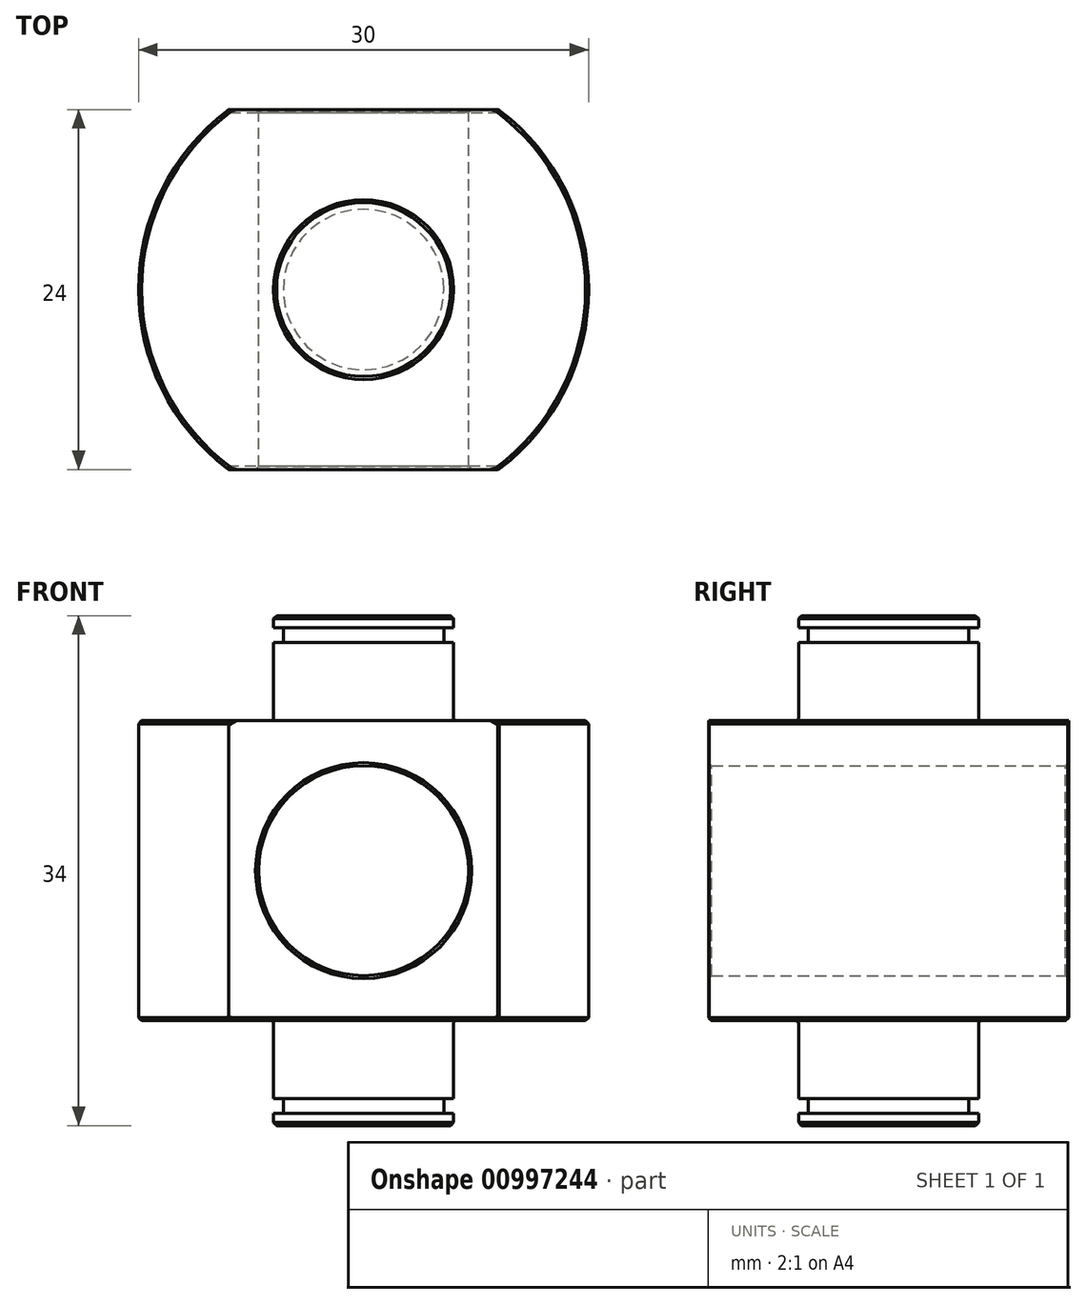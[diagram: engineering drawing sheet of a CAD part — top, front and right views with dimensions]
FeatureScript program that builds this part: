
annotation { "Feature Type Name" : "Feature", "Feature Type Description" : "" }
export const myFeature = defineFeature(function(context is Context, id is Id, definition is map)
    precondition{}
    {
        {
            var Q0;
            Q0=qCreatedBy(makeId("Front.planeOp"),FACE);
            var sketch = newSketch(context, id + "F0", { "sketchPlane" : qUnion([Q0])});
            skLineSegment(sketch, "E0", {"start": v(0, 17) * mm, "end": v(-6, 17) * mm});
            skLineSegment(sketch, "E1", {"start": v(-6, 17) * mm, "end": v(-6, 10) * mm});
            skLineSegment(sketch, "E2", {"start": v(-6, 10) * mm, "end": v(-15, 10) * mm});
            skLineSegment(sketch, "E3", {"start": v(-15, 10) * mm, "end": v(-15, -10) * mm});
            skLineSegment(sketch, "E4", {"start": v(-15, -10) * mm, "end": v(-6, -10) * mm});
            skLineSegment(sketch, "E5", {"start": v(-6, -10) * mm, "end": v(-6, -17) * mm});
            skLineSegment(sketch, "E6", {"start": v(-6, -17) * mm, "end": v(0, -17) * mm});
            skLineSegment(sketch, "E7", {"start": v(0, -17) * mm, "end": v(0, 17) * mm});
            skLineSegment(sketch, "E8", {"start": v(0, 58.87) * mm, "end": v(0, -50.94) * mm, "construction": true});
            skSolve(sketch);
        }
        {
            var Q0;
            Q0=makeQuery(id+"F0.imprint","IMPRINT",FACE,{"disambiguationData":[TD([[makeQuery(id+"F0.imprint","IMPRINT",EDGE,{"derivedFrom":sQuery(id+"F0.wireOp",EDGE,"E0")}),1.0]])]});
            var Q1;
            Q1=sQuery(id+"F0.wireOp",EDGE,"E8");
            revolve(context, id + "F1", {"surfaceOperationType" : NewSurfaceOperationType.NEW, "entities" : qUnion([Q0]), "axis" : qUnion([Q1]), "revolveType" : RevolveType.FULL});
        }
        {
            var Q0;
            Q0=makeQuery(id+"F1.opRevolve","SWEPT_EDGE",EDGE,{"disambiguationData":[OSD([sQuery(id+"F0.wireOp",EDGE,"E0"),sQuery(id+"F0.wireOp",EDGE,"E1")])]});
            var Q1;
            Q1=makeQuery(id+"F1.opRevolve","SWEPT_EDGE",EDGE,{"disambiguationData":[OSD([sQuery(id+"F0.wireOp",EDGE,"E2"),sQuery(id+"F0.wireOp",EDGE,"E3")])]});
            var Q2;
            Q2=makeQuery(id+"F1.opRevolve","SWEPT_EDGE",EDGE,{"disambiguationData":[OSD([sQuery(id+"F0.wireOp",EDGE,"E3"),sQuery(id+"F0.wireOp",EDGE,"E4")])]});
            var Q3;
            Q3=makeQuery(id+"F1.opRevolve","SWEPT_EDGE",EDGE,{"disambiguationData":[OSD([sQuery(id+"F0.wireOp",EDGE,"E5"),sQuery(id+"F0.wireOp",EDGE,"E6")])]});
            chamfer(context, id + "F2", {"entities" : qUnion([Q0, Q1, Q2, Q3]), "width" : 0.2 * mm, "tangentPropagation" : true});
        }
        {
            var Q0;
            Q0=qCreatedBy(makeId("Front.planeOp"),FACE);
            var sketch = newSketch(context, id + "F3", { "sketchPlane" : qUnion([Q0])});
            skCircle(sketch, "E9", {"center": v(0, 0) * mm, "radius": 7 * mm});
            skSolve(sketch);
        }
        {
            var Q0;
            Q0 = qSketchRegion(id + "F3", true);
            extrude(context, id + "F4", {"entities" : qUnion([Q0]), "operationType" : NewBodyOperationType.REMOVE, "depth" : 25 * mm, "offsetDistance" : 25 * mm, "hasSecondDirection" : true, "secondDirectionOppositeDirection" : true, "secondDirectionDepth" : 25 * mm});
        }
        {
            var Q0;
            Q0=makeQuery(id+"F1.opRevolve","SWEPT_FACE",FACE,{"disambiguationData":[OSD([sQuery(id+"F0.wireOp",EDGE,"E2")])]});
            cPlane(context, id + "F5", {"entities" : qUnion([Q0]), "cplaneType" : CPlaneType.OFFSET, "offset" : 0 * mm, "width" : 150 * mm, "height" : 150 * mm});
        }
        {
            var Q0;
            Q0=qCreatedBy(id+"F5.planeOp",FACE);
            var sketch = newSketch(context, id + "F6", { "sketchPlane" : qUnion([Q0])});
            skArc(sketch, "E10", {"start": v(9, 12) * mm, "mid": v(0, 15) * mm, "end": v(-9, 12) * mm});
            skLineSegment(sketch, "E11", {"start": v(-9, -12) * mm, "end": v(9, -12) * mm});
            skLineSegment(sketch, "E12", {"start": v(-9, 12) * mm, "end": v(9, 12) * mm});
            skArc(sketch, "E13.trimOffspring", {"start": v(-9, -12) * mm, "mid": v(0, -15) * mm, "end": v(9, -12) * mm});
            skSolve(sketch);
        }
        {
            var Q0;
            Q0 = qSketchRegion(id + "F6", true);
            extrude(context, id + "F7", {"entities" : qUnion([Q0]), "operationType" : NewBodyOperationType.REMOVE, "oppositeDirection" : true, "depth" : 25 * mm, "offsetDistance" : 25 * mm});
        }
        {
            var Q0;
            Q0=makeQuery(id+"F7.boolean.opBoolean","INTERSECT",EDGE,{"derivedFrom":[makeQuery(id+"F4.boolean.opBoolean","COPY",FACE,{"derivedFrom":makeQuery(id+"F4.opExtrude","SWEPT_FACE",FACE,{"disambiguationData":[OSD([sQuery(id+"F3.wireOp",EDGE,"E9")])]})}),makeQuery(id+"F7.opExtrude","SWEPT_FACE",FACE,{"disambiguationData":[OSD([sQuery(id+"F6.wireOp",EDGE,"E12")])]})]});
            var Q1;
            Q1=makeQuery(id+"F7.boolean.opBoolean","COPY",EDGE,{"derivedFrom":makeQuery(id+"F7.opExtrude","CAP_EDGE",EDGE,{"disambiguationData":[OSD([sQuery(id+"F6.wireOp",EDGE,"E12")])],"isStart":true})});
            var Q2;
            {var subQ0=sQuery(id+"F6.wireOp",EDGE,"E12");var subQ1=sQuery(id+"F6.wireOp",EDGE,"E10");Q2=makeQuery(id+"F7.boolean.opBoolean","COPY",EDGE,{"derivedFrom":makeQuery(id+"F7.opExtrude","SWEPT_EDGE",EDGE,{"disambiguationData":[OSD([subQ1,subQ0]),TDD([makeQuery(id+"F6.imprint","INTERSECT",VERTEX,{"disambiguationData":[OD(0.0)],"derivedFrom":[subQ1,subQ0]})])]})});}
            var Q3;
            Q3=makeQuery(id+"F7.boolean.opBoolean","INTERSECT",EDGE,{"derivedFrom":[makeQuery(id+"F1.opRevolve","SWEPT_FACE",FACE,{"disambiguationData":[OSD([sQuery(id+"F0.wireOp",EDGE,"E4")])]}),makeQuery(id+"F7.opExtrude","SWEPT_FACE",FACE,{"disambiguationData":[OSD([sQuery(id+"F6.wireOp",EDGE,"E12")])]})]});
            var Q4;
            {var subQ0=sQuery(id+"F6.wireOp",EDGE,"E12");var subQ1=sQuery(id+"F6.wireOp",EDGE,"E10");Q4=makeQuery(id+"F7.boolean.opBoolean","COPY",EDGE,{"derivedFrom":makeQuery(id+"F7.opExtrude","SWEPT_EDGE",EDGE,{"disambiguationData":[OSD([subQ1,subQ0]),TDD([makeQuery(id+"F6.imprint","INTERSECT",VERTEX,{"disambiguationData":[OD(1.0)],"derivedFrom":[subQ1,subQ0]})])]})});}
            var Q5;
            Q5=makeQuery(id+"F7.boolean.opBoolean","COPY",EDGE,{"derivedFrom":makeQuery(id+"F7.opExtrude","CAP_EDGE",EDGE,{"disambiguationData":[OSD([sQuery(id+"F6.wireOp",EDGE,"E11")])],"isStart":true})});
            var Q6;
            {var subQ0=sQuery(id+"F6.wireOp",EDGE,"E13.trimOffspring");var subQ1=sQuery(id+"F6.wireOp",EDGE,"E11");Q6=makeQuery(id+"F7.boolean.opBoolean","COPY",EDGE,{"derivedFrom":makeQuery(id+"F7.opExtrude","SWEPT_EDGE",EDGE,{"disambiguationData":[OSD([subQ1,subQ0]),TDD([makeQuery(id+"F6.imprint","INTERSECT",VERTEX,{"disambiguationData":[OD(1.0)],"derivedFrom":[subQ1,subQ0]})])]})});}
            var Q7;
            Q7=makeQuery(id+"F7.boolean.opBoolean","INTERSECT",EDGE,{"derivedFrom":[makeQuery(id+"F1.opRevolve","SWEPT_FACE",FACE,{"disambiguationData":[OSD([sQuery(id+"F0.wireOp",EDGE,"E4")])]}),makeQuery(id+"F7.opExtrude","SWEPT_FACE",FACE,{"disambiguationData":[OSD([sQuery(id+"F6.wireOp",EDGE,"E11")])]})]});
            var Q8;
            {var subQ0=sQuery(id+"F6.wireOp",EDGE,"E13.trimOffspring");var subQ1=sQuery(id+"F6.wireOp",EDGE,"E11");Q8=makeQuery(id+"F7.boolean.opBoolean","COPY",EDGE,{"derivedFrom":makeQuery(id+"F7.opExtrude","SWEPT_EDGE",EDGE,{"disambiguationData":[OSD([subQ1,subQ0]),TDD([makeQuery(id+"F6.imprint","INTERSECT",VERTEX,{"disambiguationData":[OD(0.0)],"derivedFrom":[subQ1,subQ0]})])]})});}
            var Q9;
            Q9=makeQuery(id+"F7.boolean.opBoolean","INTERSECT",EDGE,{"derivedFrom":[makeQuery(id+"F4.boolean.opBoolean","COPY",FACE,{"derivedFrom":makeQuery(id+"F4.opExtrude","SWEPT_FACE",FACE,{"disambiguationData":[OSD([sQuery(id+"F3.wireOp",EDGE,"E9")])]})}),makeQuery(id+"F7.opExtrude","SWEPT_FACE",FACE,{"disambiguationData":[OSD([sQuery(id+"F6.wireOp",EDGE,"E11")])]})]});
            var Q10;
            Q10=makeQuery(id+"F7.boolean.opBoolean","INTERSECT",EDGE,{"disambiguationData":[OD(1.0)],"derivedFrom":[makeQuery(id+"F2.opChamfer","BLEND_FACE",FACE,{"disambiguationData":[OSD([sQuery(id+"F0.wireOp",EDGE,"E2"),sQuery(id+"F0.wireOp",EDGE,"E3")])]}),makeQuery(id+"F7.opExtrude","SWEPT_FACE",FACE,{"disambiguationData":[OSD([sQuery(id+"F6.wireOp",EDGE,"E11")])]})]});
            var Q11;
            Q11=makeQuery(id+"F7.boolean.opBoolean","INTERSECT",EDGE,{"disambiguationData":[OD(0.0)],"derivedFrom":[makeQuery(id+"F2.opChamfer","BLEND_FACE",FACE,{"disambiguationData":[OSD([sQuery(id+"F0.wireOp",EDGE,"E2"),sQuery(id+"F0.wireOp",EDGE,"E3")])]}),makeQuery(id+"F7.opExtrude","SWEPT_FACE",FACE,{"disambiguationData":[OSD([sQuery(id+"F6.wireOp",EDGE,"E11")])]})]});
            var Q12;
            Q12=makeQuery(id+"F7.boolean.opBoolean","INTERSECT",EDGE,{"disambiguationData":[OD(0.0)],"derivedFrom":[makeQuery(id+"F2.opChamfer","BLEND_FACE",FACE,{"disambiguationData":[OSD([sQuery(id+"F0.wireOp",EDGE,"E3"),sQuery(id+"F0.wireOp",EDGE,"E4")])]}),makeQuery(id+"F7.opExtrude","SWEPT_FACE",FACE,{"disambiguationData":[OSD([sQuery(id+"F6.wireOp",EDGE,"E11")])]})]});
            var Q13;
            Q13=makeQuery(id+"F7.boolean.opBoolean","INTERSECT",EDGE,{"disambiguationData":[OD(1.0)],"derivedFrom":[makeQuery(id+"F2.opChamfer","BLEND_FACE",FACE,{"disambiguationData":[OSD([sQuery(id+"F0.wireOp",EDGE,"E3"),sQuery(id+"F0.wireOp",EDGE,"E4")])]}),makeQuery(id+"F7.opExtrude","SWEPT_FACE",FACE,{"disambiguationData":[OSD([sQuery(id+"F6.wireOp",EDGE,"E11")])]})]});
            var Q14;
            Q14=makeQuery(id+"F7.boolean.opBoolean","INTERSECT",EDGE,{"disambiguationData":[OD(0.0)],"derivedFrom":[makeQuery(id+"F2.opChamfer","BLEND_FACE",FACE,{"disambiguationData":[OSD([sQuery(id+"F0.wireOp",EDGE,"E2"),sQuery(id+"F0.wireOp",EDGE,"E3")])]}),makeQuery(id+"F7.opExtrude","SWEPT_FACE",FACE,{"disambiguationData":[OSD([sQuery(id+"F6.wireOp",EDGE,"E12")])]})]});
            var Q15;
            Q15=makeQuery(id+"F7.boolean.opBoolean","INTERSECT",EDGE,{"disambiguationData":[OD(1.0)],"derivedFrom":[makeQuery(id+"F2.opChamfer","BLEND_FACE",FACE,{"disambiguationData":[OSD([sQuery(id+"F0.wireOp",EDGE,"E2"),sQuery(id+"F0.wireOp",EDGE,"E3")])]}),makeQuery(id+"F7.opExtrude","SWEPT_FACE",FACE,{"disambiguationData":[OSD([sQuery(id+"F6.wireOp",EDGE,"E12")])]})]});
            var Q16;
            Q16=makeQuery(id+"F7.boolean.opBoolean","INTERSECT",EDGE,{"disambiguationData":[OD(0.0)],"derivedFrom":[makeQuery(id+"F2.opChamfer","BLEND_FACE",FACE,{"disambiguationData":[OSD([sQuery(id+"F0.wireOp",EDGE,"E3"),sQuery(id+"F0.wireOp",EDGE,"E4")])]}),makeQuery(id+"F7.opExtrude","SWEPT_FACE",FACE,{"disambiguationData":[OSD([sQuery(id+"F6.wireOp",EDGE,"E12")])]})]});
            var Q17;
            Q17=makeQuery(id+"F7.boolean.opBoolean","INTERSECT",EDGE,{"disambiguationData":[OD(1.0)],"derivedFrom":[makeQuery(id+"F2.opChamfer","BLEND_FACE",FACE,{"disambiguationData":[OSD([sQuery(id+"F0.wireOp",EDGE,"E3"),sQuery(id+"F0.wireOp",EDGE,"E4")])]}),makeQuery(id+"F7.opExtrude","SWEPT_FACE",FACE,{"disambiguationData":[OSD([sQuery(id+"F6.wireOp",EDGE,"E12")])]})]});
            chamfer(context, id + "F8", {"entities" : qUnion([Q0, Q1, Q2, Q3, Q4, Q5, Q6, Q7, Q8, Q9, Q10, Q11, Q12, Q13, Q14, Q15, Q16, Q17]), "width" : 0.2 * mm, "tangentPropagation" : true});
        }
        {
            var Q0;
            Q0=makeQuery(id+"F1.opRevolve","SWEPT_EDGE",EDGE,{"disambiguationData":[OSD([sQuery(id+"F0.wireOp",EDGE,"E1"),sQuery(id+"F0.wireOp",EDGE,"E2")])]});
            var Q1;
            Q1=makeQuery(id+"F1.opRevolve","SWEPT_EDGE",EDGE,{"disambiguationData":[OSD([sQuery(id+"F0.wireOp",EDGE,"E4"),sQuery(id+"F0.wireOp",EDGE,"E5")])]});
            fillet(context, id + "F9", {"entities" : qUnion([Q0, Q1]), "radius" : 0.2 * mm, "tangentPropagation" : true, "allowEdgeOverflow" : false});
        }
        {
            var Q0;
            Q0=qCreatedBy(makeId("Front.planeOp"),FACE);
            var sketch = newSketch(context, id + "F10", { "sketchPlane" : qUnion([Q0])});
            skLineSegment(sketch, "E14", {"start": v(-6, 16.2) * mm, "end": v(-5.35, 16.2) * mm});
            skLineSegment(sketch, "E15", {"start": v(-5.35, 16.2) * mm, "end": v(-5.35, 15.2) * mm});
            skLineSegment(sketch, "E16", {"start": v(-5.35, 15.2) * mm, "end": v(-6, 15.2) * mm});
            skLineSegment(sketch, "E17", {"start": v(-6, 16.2) * mm, "end": v(-6, 15.2) * mm});
            skLineSegment(sketch, "E18", {"start": v(0, 34.13) * mm, "end": v(0, -28.15) * mm, "construction": true});
            skLineSegment(sketch, "E19", {"start": v(-9.44, 0) * mm, "end": v(34, 0) * mm, "construction": true});
            skLineSegment(sketch, "E20.MirrorCS", {"start": v(-6, -16.2) * mm, "end": v(-5.35, -16.2) * mm});
            skLineSegment(sketch, "E21.MirrorCS", {"start": v(-5.35, -16.2) * mm, "end": v(-5.35, -15.2) * mm});
            skLineSegment(sketch, "E22.MirrorCS", {"start": v(-5.35, -15.2) * mm, "end": v(-6, -15.2) * mm});
            skLineSegment(sketch, "E23.MirrorCS", {"start": v(-6, -16.2) * mm, "end": v(-6, -15.2) * mm});
            skSolve(sketch);
        }
        {
            var Q0;
            Q0 = qSketchRegion(id + "F10", true);
            var Q1;
            Q1=sQuery(id+"F10.wireOp",EDGE,"E18");
            revolve(context, id + "F11", {"operationType" : NewBodyOperationType.REMOVE, "surfaceOperationType" : NewSurfaceOperationType.NEW, "entities" : qUnion([Q0]), "axis" : qUnion([Q1]), "revolveType" : RevolveType.FULL, "oppositeDirection" : true});
        }
    });
